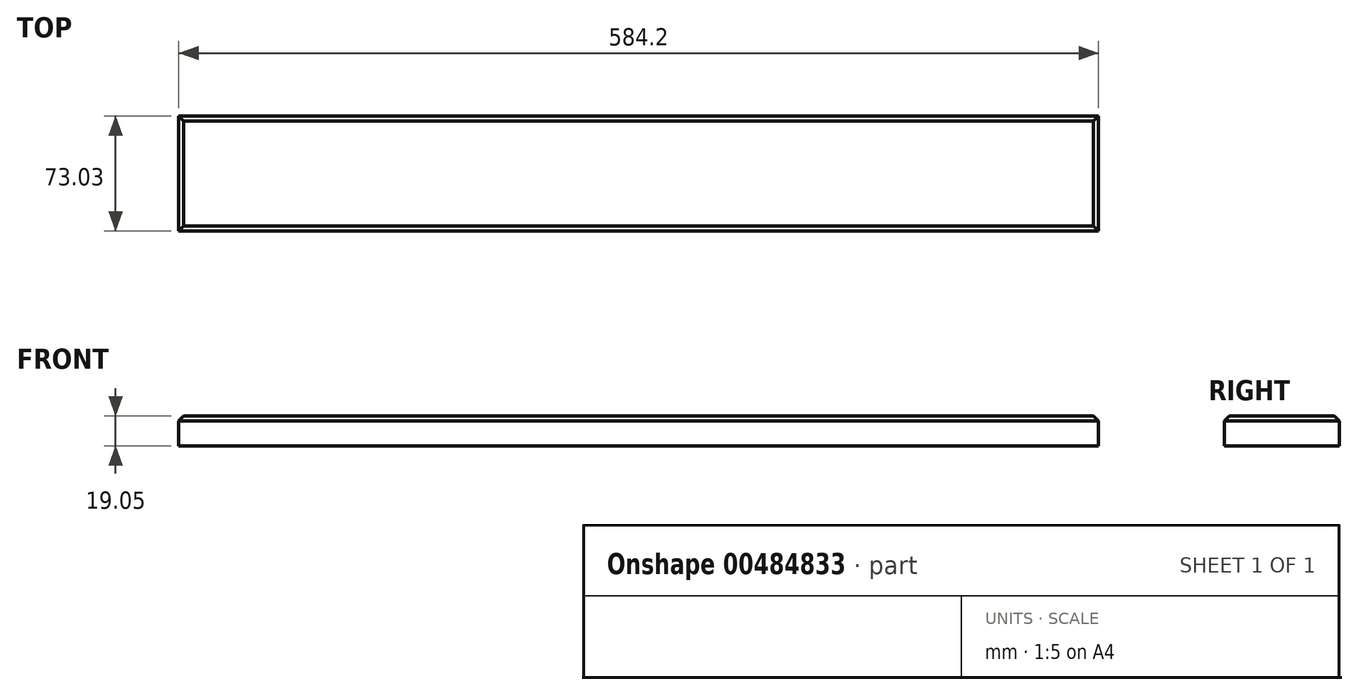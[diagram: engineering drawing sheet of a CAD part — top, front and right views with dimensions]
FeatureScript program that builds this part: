
annotation { "Feature Type Name" : "Feature", "Feature Type Description" : "" }
export const myFeature = defineFeature(function(context is Context, id is Id, definition is map)
    precondition{}
    {
        {
            var Q0;
            Q0=qCreatedBy(makeId("Top.planeOp"),FACE);
            var sketch = newSketch(context, id + "F0", { "sketchPlane" : qUnion([Q0])});
            skLineSegment(sketch, "E0.bottom", {"start": v(-132.22, 0) * mm, "end": v(451.98, 0) * mm});
            skLineSegment(sketch, "E0.top", {"start": v(-132.22, 73.03) * mm, "end": v(451.98, 73.03) * mm});
            skLineSegment(sketch, "E0.left", {"start": v(-132.22, 0) * mm, "end": v(-132.22, 73.03) * mm});
            skLineSegment(sketch, "E0.right", {"start": v(451.98, 0) * mm, "end": v(451.98, 73.03) * mm});
            skSolve(sketch);
        }
        {
            var Q0;
            Q0 = qSketchRegion(id + "F0", true);
            extrude(context, id + "F1", {"entities" : qUnion([Q0]), "depth" : 19.05 * mm});
        }
        {
            var Q0;
            Q0=makeQuery(id+"F1.opExtrude","CAP_EDGE",EDGE,{"disambiguationData":[OSD([sQuery(id+"F0.wireOp",EDGE,"E0.top")])],"isStart":false});
            var Q1;
            Q1=makeQuery(id+"F1.opExtrude","CAP_EDGE",EDGE,{"disambiguationData":[OSD([sQuery(id+"F0.wireOp",EDGE,"E0.left")])],"isStart":false});
            var Q2;
            Q2=makeQuery(id+"F1.opExtrude","CAP_EDGE",EDGE,{"disambiguationData":[OSD([sQuery(id+"F0.wireOp",EDGE,"E0.bottom")])],"isStart":false});
            var Q3;
            Q3=makeQuery(id+"F1.opExtrude","CAP_EDGE",EDGE,{"disambiguationData":[OSD([sQuery(id+"F0.wireOp",EDGE,"E0.right")])],"isStart":false});
            chamfer(context, id + "F2", {"entities" : qUnion([Q0, Q1, Q2, Q3]), "width" : 3.17 * mm, "tangentPropagation" : true});
        }
    });
